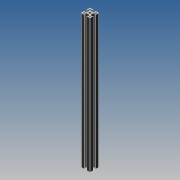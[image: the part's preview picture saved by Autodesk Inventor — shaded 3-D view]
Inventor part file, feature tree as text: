
AUTODESK INVENTOR PART (.ipt)
format: ipt  version: 2019 (Build 230136000, 136)  size: 261,120 bytes
history: native  units: mm
features: extrude x1, sketch x1, projected_geometry x1, other x1
ambient origin geometry x8: Origin, YZ Plane, XZ Plane, XY Plane, X Axis, Y Axis, Z Axis, Center Point
bodies: Solid1 (feature_tree)
feature tree (4):
  extrude  "Extrusion1"  [1 undecoded]
  sketch  "Sketch1"  dims[d0=150.0mm d1=0.0mm]
  projected_geometry  "Projected Loop1"
  parser-record x1  (decoder bookkeeping rows leaked as tree rows — omitted from the tree; the rows remain in map.json)
note: 1 required parameter value undecoded (feature->parameter linkage not recoverable at this tier; creation-order binding heuristic only, values carry confidence <= 0.55)
